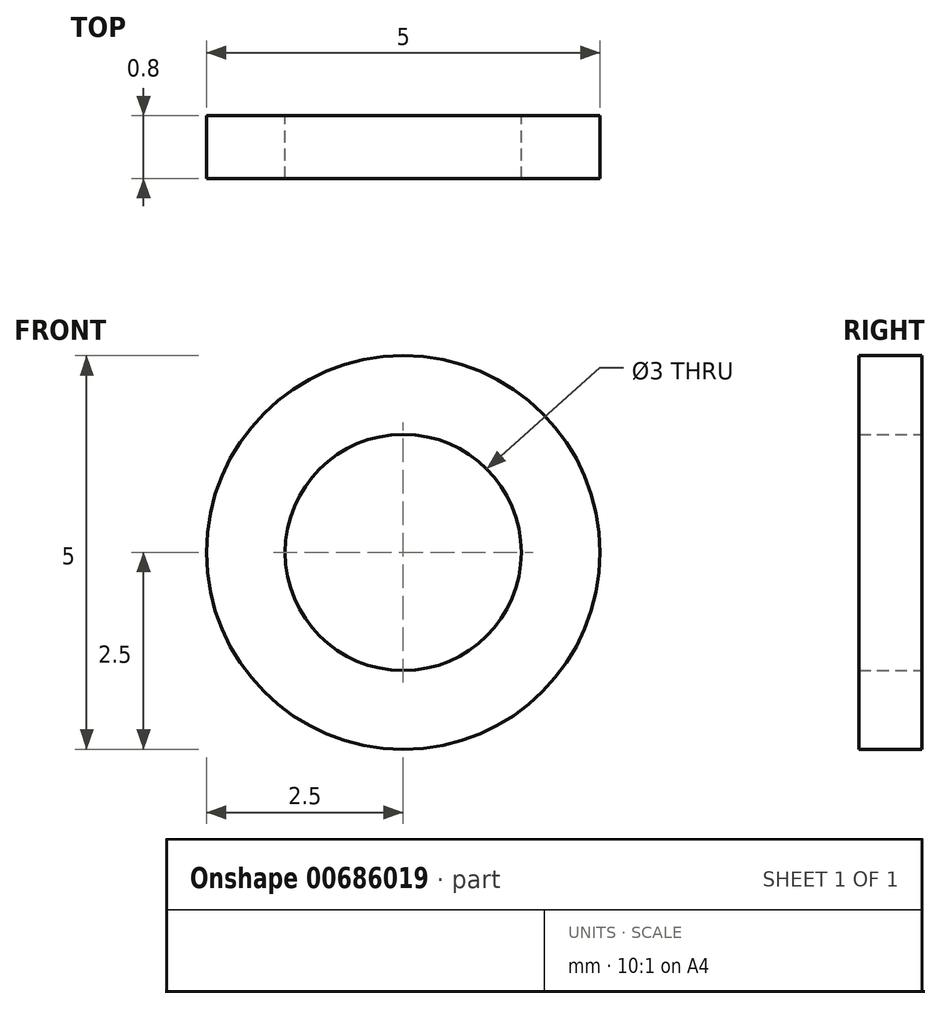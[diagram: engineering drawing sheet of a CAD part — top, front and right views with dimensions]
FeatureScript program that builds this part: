
annotation { "Feature Type Name" : "Feature", "Feature Type Description" : "" }
export const myFeature = defineFeature(function(context is Context, id is Id, definition is map)
    precondition{}
    {
        {
            var Q0;
            Q0=qCreatedBy(makeId("Front.planeOp"),FACE);
            var sketch = newSketch(context, id + "F0", { "sketchPlane" : qUnion([Q0])});
            skCircle(sketch, "E0", {"center": v(0, 0) * mm, "radius": 2.5 * mm});
            skCircle(sketch, "E1", {"center": v(0, 0) * mm, "radius": 1.5 * mm});
            skSolve(sketch);
        }
        {
            var Q0;
            Q0=makeQuery(id+"F0.imprint","IMPRINT",FACE,{"disambiguationData":[TD([[makeQuery(id+"F0.imprint","IMPRINT",EDGE,{"derivedFrom":sQuery(id+"F0.wireOp",EDGE,"E0")}),1.0]])]});
            extrude(context, id + "F1", {"entities" : qUnion([Q0]), "depth" : .8 * mm, "offsetDistance" : 25 * mm});
        }
    });
